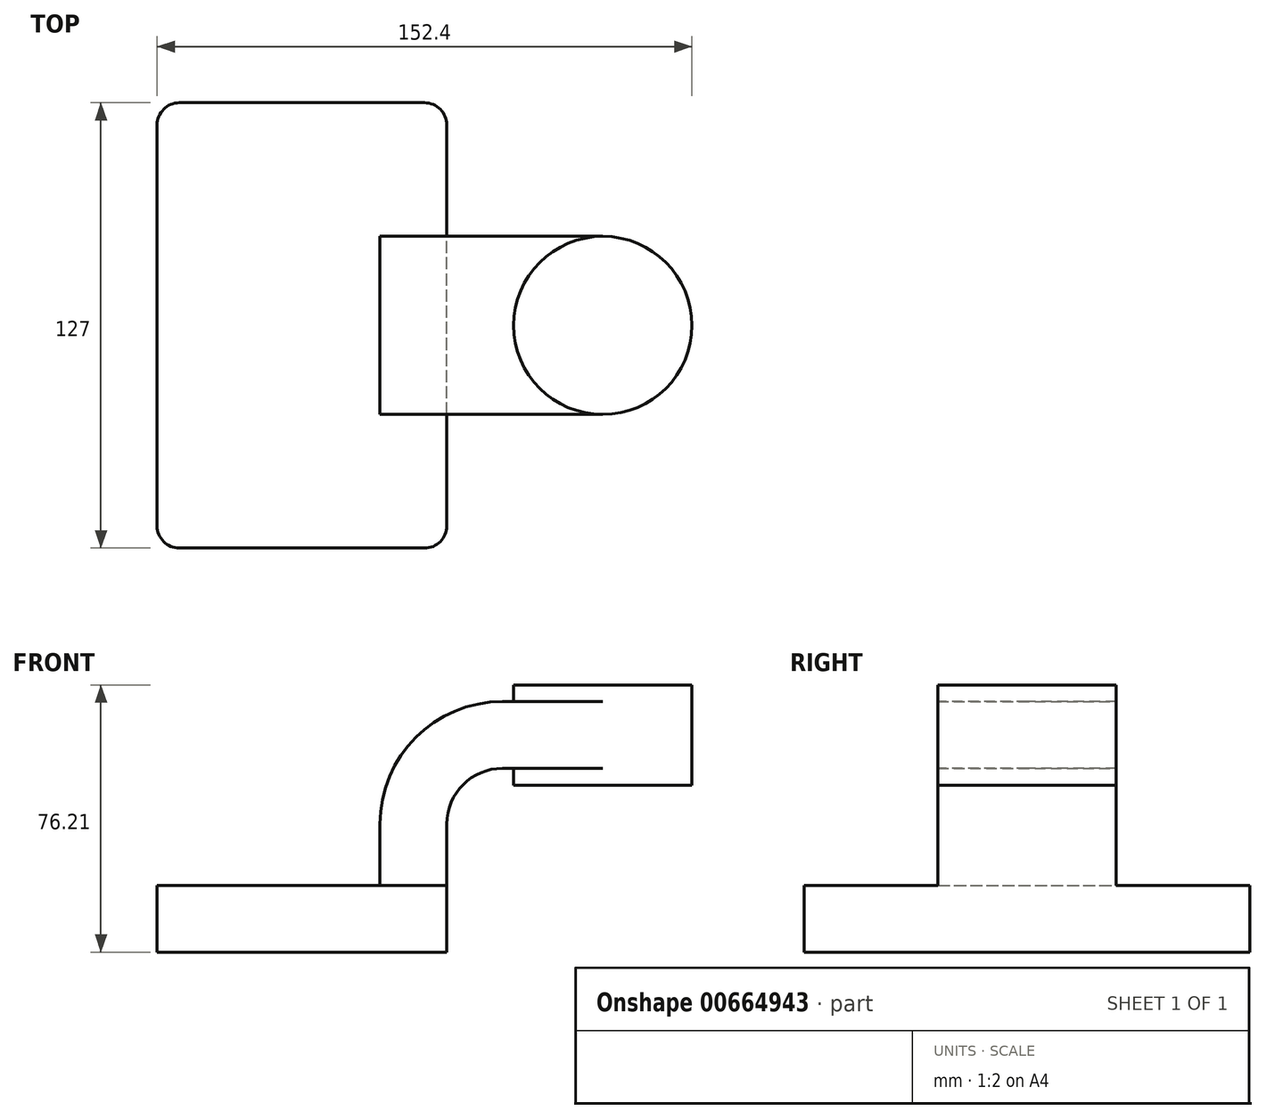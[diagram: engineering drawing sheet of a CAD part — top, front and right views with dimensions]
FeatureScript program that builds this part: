
annotation { "Feature Type Name" : "Feature", "Feature Type Description" : "" }
export const myFeature = defineFeature(function(context is Context, id is Id, definition is map)
    precondition{}
    {
        {
            var Q0;
            Q0=qCreatedBy(makeId("Front.planeOp"),FACE);
            var sketch = newSketch(context, id + "F0", { "sketchPlane" : qUnion([Q0])});
            skLineSegment(sketch, "E0.bottom", {"start": v(41.28, -9.52) * mm, "end": v(-41.28, -9.53) * mm});
            skLineSegment(sketch, "E0.top", {"start": v(41.28, 9.53) * mm, "end": v(-41.28, 9.53) * mm});
            skLineSegment(sketch, "E0.left", {"start": v(41.28, -9.52) * mm, "end": v(41.27, 9.53) * mm});
            skLineSegment(sketch, "E0.right", {"start": v(-41.28, -9.53) * mm, "end": v(-41.28, 9.52) * mm});
            skPoint(sketch, "E0.middle", {"position": v(0, 0) * mm});
            skLineSegment(sketch, "E1.bottom", {"start": v(60.32, 66.68) * mm, "end": v(111.12, 66.68) * mm});
            skLineSegment(sketch, "E1.top", {"start": v(60.32, 38.1) * mm, "end": v(111.12, 38.1) * mm});
            skLineSegment(sketch, "E1.left", {"start": v(60.32, 66.68) * mm, "end": v(60.32, 38.1) * mm});
            skLineSegment(sketch, "E1.right", {"start": v(111.12, 66.68) * mm, "end": v(111.12, 38.1) * mm});
            skPoint(sketch, "E2.endSnap0", {"position": v(60.32, 52.39) * mm});
            skLineSegment(sketch, "E3", {"start": v(41.28, 9.53) * mm, "end": v(41.28, 27) * mm});
            skArc(sketch, "E4", {"start": v(41.27, 27) * mm, "mid": v(45.92, 38.23) * mm, "end": v(57.15, 42.88) * mm});
            skLineSegment(sketch, "E5", {"start": v(57.15, 42.88) * mm, "end": v(85.72, 42.88) * mm});
            skLineSegment(sketch, "E6", {"start": v(85.72, 38.1) * mm, "end": v(85.72, 66.68) * mm});
            skLineSegment(sketch, "E7.0", {"start": v(57.15, 61.93) * mm, "end": v(85.72, 61.93) * mm});
            skArc(sketch, "E7.1", {"start": v(22.23, 27) * mm, "mid": v(32.45, 51.7) * mm, "end": v(57.15, 61.93) * mm});
            skLineSegment(sketch, "E7.2", {"start": v(22.23, 9.53) * mm, "end": v(22.23, 27) * mm});
            skFitSpline(sketch, "E8", {"points": [v(-41.28, 9.52) * mm, v(57.15, 61.93) * mm], "startDerivative": vector(1.07, 41.98) * mm, "endDerivative": vector(114.94, -11.86) * mm});
            skSolve(sketch);
        }
        {
            var Q0;
            Q0=makeQuery(id+"F0.imprint","IMPRINT",FACE,{"disambiguationData":[TD([[makeQuery(id+"F0.imprint","IMPRINT",EDGE,{"derivedFrom":sQuery(id+"F0.wireOp",EDGE,"E0.bottom")}),-1.0]])]});
            extrude(context, id + "F1", {"entities" : qUnion([Q0]), "endBound" : BoundingType.SYMMETRIC, "depth" : 127 * mm, "offsetDistance" : 25.4 * mm});
        }
        {
            var Q0;
            {var subQ1=sQuery(id+"F0.wireOp",EDGE,"E3");Q0=makeQuery(id+"F0.imprint","IMPRINT",FACE,{"disambiguationData":[TD([[makeQuery(id+"F0.imprint","IMPRINT",EDGE,{"derivedFrom":subQ1}),1.0]])]});}
            var Q1;
            {var subQ0=sQuery(id+"F0.wireOp",EDGE,"E7.0");var subQ1=sQuery(id+"F0.wireOp",EDGE,"E1.left");var subQ2=makeQuery(id+"F0.imprint","INTERSECT",VERTEX,{"derivedFrom":[subQ1,subQ0]});Q1=makeQuery(id+"F0.imprint","IMPRINT",FACE,{"disambiguationData":[TD([[makeQuery(id+"F0.imprint","IMPRINT",EDGE,{"disambiguationData":[TD([[subQ2,-1.0]])],"derivedFrom":subQ1}),1.0]])]});}
            extrude(context, id + "F2", {"entities" : qUnion([Q0, Q1]), "operationType" : NewBodyOperationType.ADD, "endBound" : BoundingType.SYMMETRIC, "depth" : 50.8 * mm, "offsetDistance" : 25.4 * mm});
        }
        {
            var Q0;
            Q0=makeQuery(id+"F0.imprint","IMPRINT",FACE,{"disambiguationData":[TD([[makeQuery(id+"F0.imprint","IMPRINT",EDGE,{"derivedFrom":sQuery(id+"F0.wireOp",EDGE,"E7.1")}),1.0]])]});
            extrude(context, id + "F3", {"entities" : qUnion([Q0]), "operationType" : NewBodyOperationType.ADD, "endBound" : BoundingType.SYMMETRIC, "depth" : 15.88 * mm, "offsetDistance" : 25.4 * mm});
        }
        {
            var Q0;
            {var subQ4=sQuery(id+"F0.wireOp",EDGE,"E1.right");Q0=makeQuery(id+"F0.imprint","IMPRINT",FACE,{"disambiguationData":[TD([[makeQuery(id+"F0.imprint","IMPRINT",EDGE,{"derivedFrom":subQ4}),-1.0]])]});}
            var Q1;
            Q1=sQuery(id+"F0.wireOp",EDGE,"E6");
            revolve(context, id + "F4", {"operationType" : NewBodyOperationType.ADD, "entities" : qUnion([Q0]), "axis" : qUnion([Q1]), "revolveType" : RevolveType.FULL});
        }
        {
            var Q0;
            Q0=makeQuery(id+"F1.opExtrude","CAP_EDGE",EDGE,{"disambiguationData":[OSD([sQuery(id+"F0.wireOp",EDGE,"E0.left")])],"isStart":false});
            var Q1;
            Q1=makeQuery(id+"F1.opExtrude","CAP_EDGE",EDGE,{"disambiguationData":[OSD([sQuery(id+"F0.wireOp",EDGE,"E0.right")])],"isStart":false});
            var Q2;
            Q2=makeQuery(id+"F1.opExtrude","CAP_EDGE",EDGE,{"disambiguationData":[OSD([sQuery(id+"F0.wireOp",EDGE,"E0.left")])],"isStart":true});
            var Q3;
            Q3=makeQuery(id+"F1.opExtrude","CAP_EDGE",EDGE,{"disambiguationData":[OSD([sQuery(id+"F0.wireOp",EDGE,"E0.right")])],"isStart":true});
            fillet(context, id + "F5", {"entities" : qUnion([Q0, Q1, Q2, Q3]), "radius" : 6.35 * mm, "tangentPropagation" : true, "allowEdgeOverflow" : false});
        }
    });
